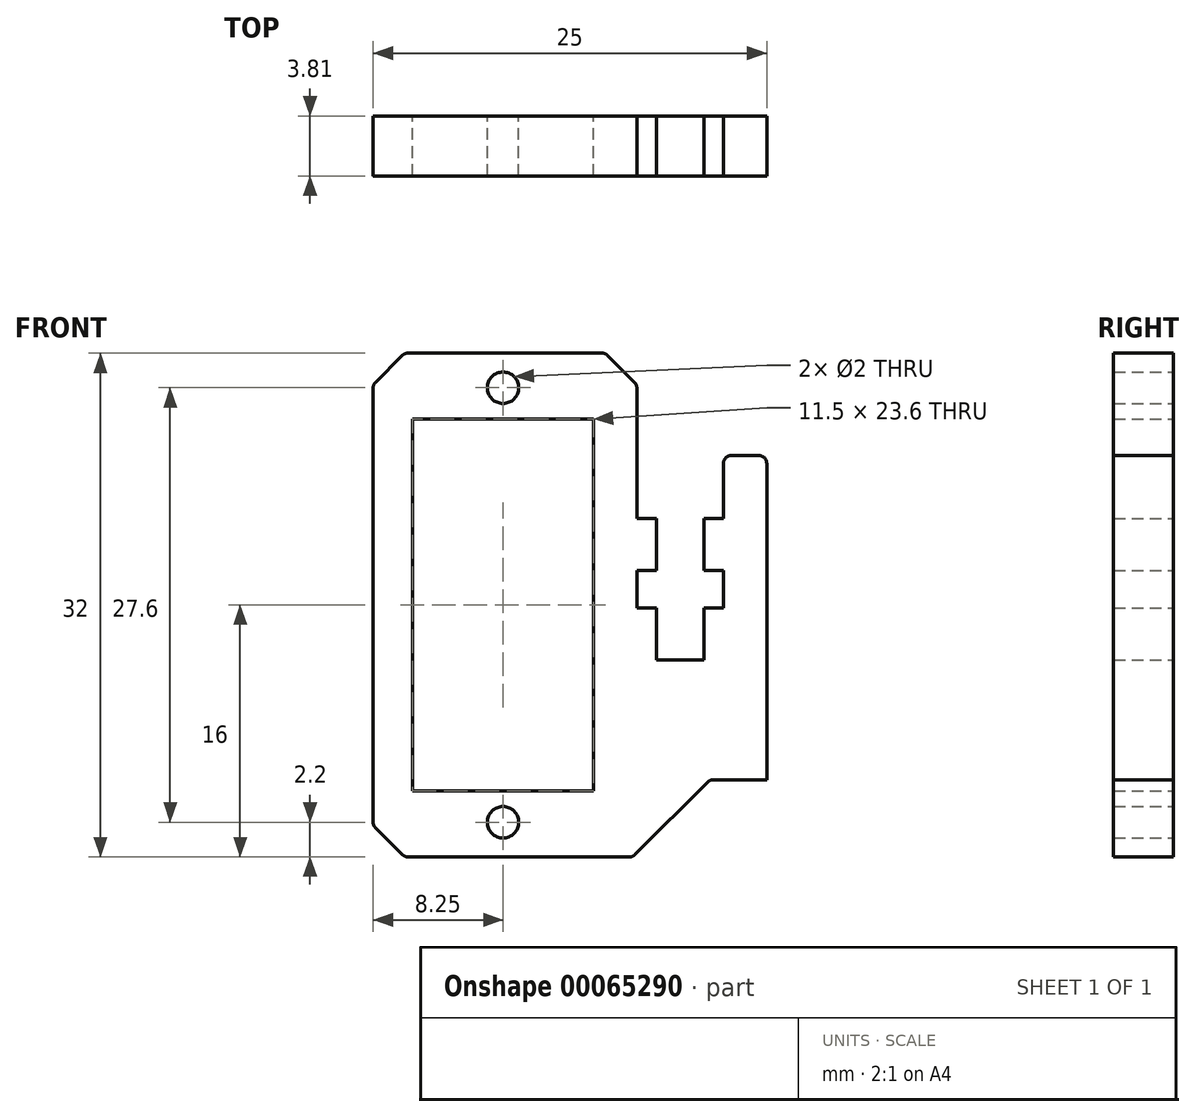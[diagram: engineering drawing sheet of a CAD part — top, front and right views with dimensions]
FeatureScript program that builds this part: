
annotation { "Feature Type Name" : "Feature", "Feature Type Description" : "" }
export const myFeature = defineFeature(function(context is Context, id is Id, definition is map)
    precondition{}
    {
        {
            var Q0;
            Q0=qCreatedBy(makeId("Front.planeOp"),FACE);
            var sketch = newSketch(context, id + "F0", { "sketchPlane" : qUnion([Q0])});
            skArc(sketch, "E0", {"start": v(12.5, 9) * mm, "mid": v(12.35, 9.35) * mm, "end": v(12, 9.5) * mm});
            skArc(sketch, "E1", {"start": v(9.1, -11.1) * mm, "mid": v(8.92, -11.14) * mm, "end": v(8.75, -11.25) * mm});
            skArc(sketch, "E2", {"start": v(3.8, -16) * mm, "mid": v(3.98, -15.96) * mm, "end": v(4.15, -15.85) * mm});
            skArc(sketch, "E3", {"start": v(-10.65, -15.85) * mm, "mid": v(-10.48, -15.96) * mm, "end": v(-10.3, -16) * mm});
            skLineSegment(sketch, "E4", {"start": v(-12.35, -14.15) * mm, "end": v(-10.65, -15.85) * mm});
            skArc(sketch, "E5", {"start": v(-12.5, -13.8) * mm, "mid": v(-12.46, -13.98) * mm, "end": v(-12.35, -14.15) * mm});
            skArc(sketch, "E6", {"start": v(-12.35, 14.15) * mm, "mid": v(-12.46, 13.98) * mm, "end": v(-12.5, 13.8) * mm});
            skLineSegment(sketch, "E7", {"start": v(-10.65, 15.85) * mm, "end": v(-12.35, 14.15) * mm});
            skArc(sketch, "E8", {"start": v(-10.3, 16) * mm, "mid": v(-10.48, 15.96) * mm, "end": v(-10.65, 15.85) * mm});
            skArc(sketch, "E9", {"start": v(2.4, 15.85) * mm, "mid": v(2.23, 15.96) * mm, "end": v(2.04, 16) * mm});
            skLineSegment(sketch, "E10", {"start": v(4.1, 14.15) * mm, "end": v(2.4, 15.85) * mm});
            skArc(sketch, "E11", {"start": v(4.25, 13.8) * mm, "mid": v(4.21, 13.98) * mm, "end": v(4.1, 14.15) * mm});
            skArc(sketch, "E12", {"start": v(10.25, 9.5) * mm, "mid": v(9.9, 9.35) * mm, "end": v(9.75, 9) * mm});
            skCircle(sketch, "E13", {"center": v(-4.25, -13.8) * mm, "radius": 1 * mm});
            skLineSegment(sketch, "E14", {"start": v(8.5, -3.5) * mm, "end": v(5.5, -3.5) * mm});
            skLineSegment(sketch, "E15", {"start": v(1.5, 11.8) * mm, "end": v(1.5, -11.8) * mm});
            skCircle(sketch, "E16", {"center": v(-4.25, 13.8) * mm, "radius": 1 * mm});
            skLineSegment(sketch, "E17", {"start": v(8.5, -3.5) * mm, "end": v(8.5, -0.2) * mm});
            skLineSegment(sketch, "E18", {"start": v(9.75, -0.2) * mm, "end": v(8.5, -0.2) * mm});
            skLineSegment(sketch, "E19", {"start": v(9.75, -0.2) * mm, "end": v(9.75, 2.2) * mm});
            skLineSegment(sketch, "E20", {"start": v(9.75, 2.2) * mm, "end": v(8.5, 2.2) * mm});
            skLineSegment(sketch, "E21", {"start": v(8.5, 2.2) * mm, "end": v(8.5, 5.5) * mm});
            skLineSegment(sketch, "E22", {"start": v(8.5, 5.5) * mm, "end": v(9.75, 5.5) * mm});
            skLineSegment(sketch, "E23", {"start": v(9.75, 5.5) * mm, "end": v(9.75, 9) * mm});
            skLineSegment(sketch, "E24", {"start": v(10.25, 9.5) * mm, "end": v(12, 9.5) * mm});
            skLineSegment(sketch, "E25", {"start": v(12.5, 9) * mm, "end": v(12.5, -11.1) * mm});
            skLineSegment(sketch, "E26", {"start": v(12.5, -11.1) * mm, "end": v(9.1, -11.1) * mm});
            skLineSegment(sketch, "E27", {"start": v(8.75, -11.25) * mm, "end": v(4.15, -15.85) * mm});
            skLineSegment(sketch, "E28", {"start": v(-10.3, -16) * mm, "end": v(3.8, -16) * mm});
            skLineSegment(sketch, "E29", {"start": v(-12.5, 13.8) * mm, "end": v(-12.5, -13.8) * mm});
            skLineSegment(sketch, "E30", {"start": v(-10.3, 16) * mm, "end": v(2.04, 16) * mm});
            skLineSegment(sketch, "E31", {"start": v(4.25, 13.8) * mm, "end": v(4.25, 5.5) * mm});
            skLineSegment(sketch, "E32", {"start": v(5.5, 5.5) * mm, "end": v(4.25, 5.5) * mm});
            skLineSegment(sketch, "E33", {"start": v(5.5, 2.2) * mm, "end": v(5.5, 5.5) * mm});
            skLineSegment(sketch, "E34", {"start": v(5.5, 2.2) * mm, "end": v(4.25, 2.2) * mm});
            skLineSegment(sketch, "E35", {"start": v(4.25, -0.2) * mm, "end": v(4.25, 2.2) * mm});
            skLineSegment(sketch, "E36", {"start": v(5.5, -0.2) * mm, "end": v(4.25, -0.2) * mm});
            skLineSegment(sketch, "E37", {"start": v(5.5, -3.5) * mm, "end": v(5.5, -0.2) * mm});
            skLineSegment(sketch, "E38", {"start": v(-10, 11.8) * mm, "end": v(1.5, 11.8) * mm});
            skLineSegment(sketch, "E39", {"start": v(-10, 11.8) * mm, "end": v(-10, -11.8) * mm});
            skLineSegment(sketch, "E40", {"start": v(-10, -11.8) * mm, "end": v(1.5, -11.8) * mm});
            skLineSegment(sketch, "E41", {"start": v(-4.25, 13.8) * mm, "end": v(-4.25, 16.3) * mm});
            skLineSegment(sketch, "E42", {"start": v(-4.25, 13.8) * mm, "end": v(-6.75, 13.8) * mm});
            skLineSegment(sketch, "E43", {"start": v(-4.25, 13.8) * mm, "end": v(-4.25, 11.3) * mm});
            skLineSegment(sketch, "E44", {"start": v(-4.25, 13.8) * mm, "end": v(-1.75, 13.8) * mm});
            skLineSegment(sketch, "E45", {"start": v(-4.25, 16.3) * mm, "end": v(-4.25, 17.3) * mm});
            skLineSegment(sketch, "E46", {"start": v(-6.75, 13.8) * mm, "end": v(-7.75, 13.8) * mm});
            skLineSegment(sketch, "E47", {"start": v(-4.25, 11.3) * mm, "end": v(-4.25, 10.3) * mm});
            skLineSegment(sketch, "E48", {"start": v(-1.75, 13.8) * mm, "end": v(-0.75, 13.8) * mm});
            skLineSegment(sketch, "E49", {"start": v(-4.25, -13.8) * mm, "end": v(-4.25, -11.3) * mm});
            skLineSegment(sketch, "E50", {"start": v(-4.25, -13.8) * mm, "end": v(-6.75, -13.8) * mm});
            skLineSegment(sketch, "E51", {"start": v(-4.25, -13.8) * mm, "end": v(-4.25, -16.3) * mm});
            skLineSegment(sketch, "E52", {"start": v(-4.25, -13.8) * mm, "end": v(-1.75, -13.8) * mm});
            skLineSegment(sketch, "E53", {"start": v(-4.25, -11.3) * mm, "end": v(-4.25, -10.3) * mm});
            skLineSegment(sketch, "E54", {"start": v(-6.75, -13.8) * mm, "end": v(-7.75, -13.8) * mm});
            skLineSegment(sketch, "E55", {"start": v(-4.25, -16.3) * mm, "end": v(-4.25, -17.3) * mm});
            skLineSegment(sketch, "E56", {"start": v(-1.75, -13.8) * mm, "end": v(-0.75, -13.8) * mm});
            skSolve(sketch);
        }
        {
            var Q0;
            {var subQ17=sQuery(id+"F0.wireOp",EDGE,"E3");Q0=makeQuery(id+"F0.imprint","IMPRINT",FACE,{"disambiguationData":[TD([[makeQuery(id+"F0.imprint","IMPRINT",EDGE,{"derivedFrom":subQ17}),1.0]])]});}
            var Q1;
            Q1=makeQuery(id+"F0.imprint","IMPRINT",FACE,{"disambiguationData":[TD([[makeQuery(id+"F0.imprint","IMPRINT",EDGE,{"derivedFrom":sQuery(id+"F0.wireOp",EDGE,"E0")}),1.0]])]});
            extrude(context, id + "F1", {"entities" : qUnion([Q0, Q1]), "depth" : 3.8 * mm});
        }
    });
